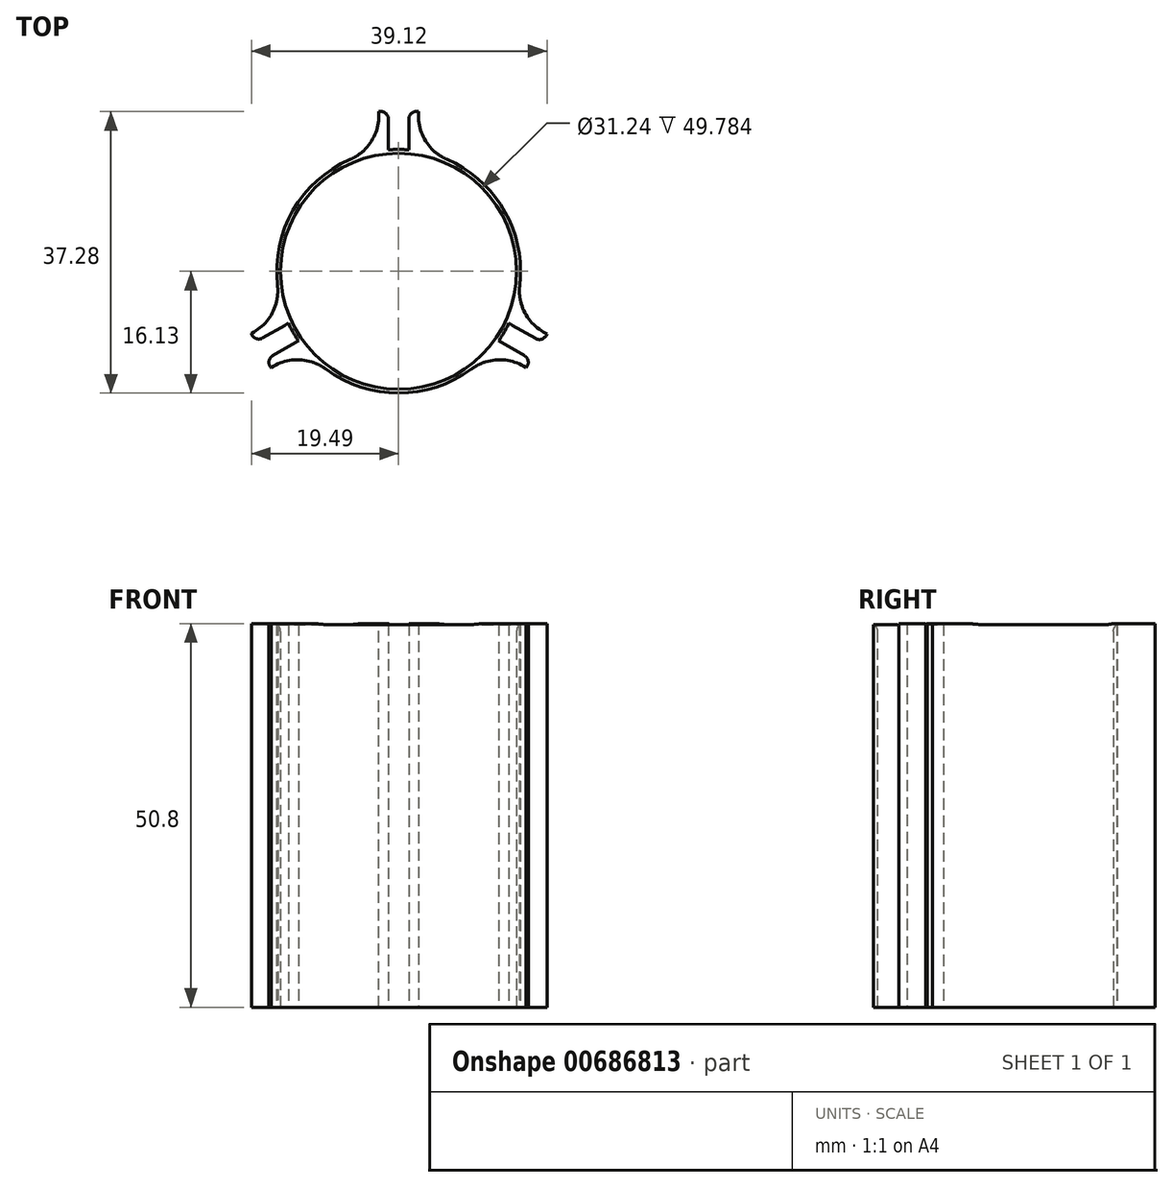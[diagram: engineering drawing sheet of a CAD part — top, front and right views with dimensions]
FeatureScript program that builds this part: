
annotation { "Feature Type Name" : "Feature", "Feature Type Description" : "" }
export const myFeature = defineFeature(function(context is Context, id is Id, definition is map)
    precondition{}
    {
        {
            var Q0;
            Q0=qCreatedBy(makeId("Top.planeOp"),FACE);
            var sketch = newSketch(context, id + "F0", { "sketchPlane" : qUnion([Q0])});
            skCircle(sketch, "E0", {"center": v(0, 0) * mm, "radius": 15.62 * mm});
            skCircle(sketch, "E1", {"center": v(0, 0) * mm, "radius": 16.13 * mm});
            skLineSegment(sketch, "E2", {"start": v(0, 0) * mm, "end": v(0, 29.54) * mm});
            skLineSegment(sketch, "E3", {"start": v(0, 0) * mm, "end": v(-29.92, -17.28) * mm});
            skLineSegment(sketch, "E4", {"start": v(0, 0) * mm, "end": v(27.94, -16.13) * mm});
            skLineSegment(sketch, "E5", {"start": v(-14.6, -6.87) * mm, "end": v(-19, -9.41) * mm});
            skLineSegment(sketch, "E6", {"start": v(-17.65, -11.74) * mm, "end": v(-13.25, -9.2) * mm});
            skPoint(sketch, "E7", {"position": v(-13.97, -8.06) * mm});
            skLineSegment(sketch, "E8", {"start": v(-15.09, -5.7) * mm, "end": v(-19.49, -8.24) * mm});
            skLineSegment(sketch, "E9", {"start": v(-19.49, -8.24) * mm, "end": v(-19, -9.41) * mm});
            skLineSegment(sketch, "E10", {"start": v(-12.48, -10.21) * mm, "end": v(-16.88, -12.75) * mm});
            skLineSegment(sketch, "E11", {"start": v(-17.65, -11.74) * mm, "end": v(-16.88, -12.75) * mm});
            skLineSegment(sketch, "E12", {"start": v(13.25, -9.2) * mm, "end": v(17.65, -11.74) * mm});
            skLineSegment(sketch, "E13", {"start": v(12.48, -10.21) * mm, "end": v(16.88, -12.75) * mm});
            skLineSegment(sketch, "E14", {"start": v(17.65, -11.74) * mm, "end": v(16.88, -12.75) * mm});
            skLineSegment(sketch, "E15", {"start": v(14.6, -6.87) * mm, "end": v(19, -9.41) * mm});
            skLineSegment(sketch, "E16", {"start": v(19, -9.41) * mm, "end": v(19.63, -8.31) * mm});
            skLineSegment(sketch, "E17", {"start": v(19.63, -8.31) * mm, "end": v(15.1, -5.7) * mm});
            skPoint(sketch, "E18", {"position": v(13.97, -8.06) * mm});
            skLineSegment(sketch, "E19", {"start": v(-1.35, 16.07) * mm, "end": v(-1.35, 21.15) * mm});
            skLineSegment(sketch, "E20", {"start": v(-1.35, 21.15) * mm, "end": v(-2.62, 21.15) * mm});
            skLineSegment(sketch, "E21", {"start": v(-2.62, 21.15) * mm, "end": v(-2.62, 15.92) * mm});
            skLineSegment(sketch, "E22", {"start": v(1.35, 16.07) * mm, "end": v(1.35, 21.15) * mm});
            skLineSegment(sketch, "E23", {"start": v(1.35, 21.15) * mm, "end": v(2.62, 21.15) * mm});
            skLineSegment(sketch, "E24", {"start": v(2.62, 21.15) * mm, "end": v(2.62, 15.92) * mm});
            skPoint(sketch, "E25", {"position": v(0, 16.13) * mm});
            skPoint(sketch, "E26", {"position": v(-1.35, 16.07) * mm});
            skSolve(sketch);
        }
        {
            var Q0;
            {var subQ0=sQuery(id+"F0.wireOp",EDGE,"E19");Q0=makeQuery(id+"F0.imprint","IMPRINT",FACE,{"disambiguationData":[TD([[makeQuery(id+"F0.imprint","IMPRINT",EDGE,{"derivedFrom":subQ0}),1.0]])]});}
            var Q1;
            {var subQ0=sQuery(id+"F0.wireOp",EDGE,"E22");Q1=makeQuery(id+"F0.imprint","IMPRINT",FACE,{"disambiguationData":[TD([[makeQuery(id+"F0.imprint","IMPRINT",EDGE,{"derivedFrom":subQ0}),-1.0]])]});}
            var Q2;
            {var subQ5=sQuery(id+"F0.wireOp",EDGE,"E2");var subQ8=sQuery(id+"F0.wireOp",EDGE,"E0");var subQ9=makeQuery(id+"F0.imprint","INTERSECT",VERTEX,{"derivedFrom":[subQ8,subQ5]});Q2=makeQuery(id+"F0.imprint","IMPRINT",FACE,{"disambiguationData":[TD([[makeQuery(id+"F0.imprint","IMPRINT",EDGE,{"disambiguationData":[TD([[subQ9,1.0]])],"derivedFrom":subQ8}),-1.0]])]});}
            var Q3;
            {var subQ0=sQuery(id+"F0.wireOp",EDGE,"E15");Q3=makeQuery(id+"F0.imprint","IMPRINT",FACE,{"disambiguationData":[TD([[makeQuery(id+"F0.imprint","IMPRINT",EDGE,{"derivedFrom":subQ0}),1.0]])]});}
            var Q4;
            {var subQ0=sQuery(id+"F0.wireOp",EDGE,"E12");Q4=makeQuery(id+"F0.imprint","IMPRINT",FACE,{"disambiguationData":[TD([[makeQuery(id+"F0.imprint","IMPRINT",EDGE,{"derivedFrom":subQ0}),-1.0]])]});}
            var Q5;
            {var subQ3=sQuery(id+"F0.wireOp",EDGE,"E3");var subQ4=sQuery(id+"F0.wireOp",EDGE,"E0");var subQ5=makeQuery(id+"F0.imprint","INTERSECT",VERTEX,{"derivedFrom":[subQ4,subQ3]});Q5=makeQuery(id+"F0.imprint","IMPRINT",FACE,{"disambiguationData":[TD([[makeQuery(id+"F0.imprint","IMPRINT",EDGE,{"disambiguationData":[TD([[subQ5,-1.0]])],"derivedFrom":subQ4}),-1.0]])]});}
            var Q6;
            {var subQ0=sQuery(id+"F0.wireOp",EDGE,"E6");Q6=makeQuery(id+"F0.imprint","IMPRINT",FACE,{"disambiguationData":[TD([[makeQuery(id+"F0.imprint","IMPRINT",EDGE,{"derivedFrom":subQ0}),-1.0]])]});}
            var Q7;
            {var subQ6=sQuery(id+"F0.wireOp",EDGE,"E3");var subQ7=sQuery(id+"F0.wireOp",EDGE,"E0");var subQ8=makeQuery(id+"F0.imprint","INTERSECT",VERTEX,{"derivedFrom":[subQ7,subQ6]});Q7=makeQuery(id+"F0.imprint","IMPRINT",FACE,{"disambiguationData":[TD([[makeQuery(id+"F0.imprint","IMPRINT",EDGE,{"disambiguationData":[TD([[subQ8,1.0]])],"derivedFrom":subQ7}),-1.0]])]});}
            var Q8;
            {var subQ0=sQuery(id+"F0.wireOp",EDGE,"E5");Q8=makeQuery(id+"F0.imprint","IMPRINT",FACE,{"disambiguationData":[TD([[makeQuery(id+"F0.imprint","IMPRINT",EDGE,{"derivedFrom":subQ0}),-1.0]])]});}
            extrude(context, id + "F1", {"entities" : qUnion([Q0, Q1, Q2, Q3, Q4, Q5, Q6, Q7, Q8]), "depth" : 50.8 * mm, "offsetDistance" : 25.4 * mm});
        }
        {
            var Q0;
            Q0=makeQuery(id+"F1.opExtrude","SWEPT_EDGE",EDGE,{"disambiguationData":[OSD([sQuery(id+"F0.wireOp",EDGE,"E1"),sQuery(id+"F0.wireOp",EDGE,"E24")])]});
            var Q1;
            Q1=makeQuery(id+"F1.opExtrude","SWEPT_EDGE",EDGE,{"disambiguationData":[OSD([sQuery(id+"F0.wireOp",EDGE,"E1"),sQuery(id+"F0.wireOp",EDGE,"E17")])]});
            var Q2;
            Q2=makeQuery(id+"F1.opExtrude","SWEPT_EDGE",EDGE,{"disambiguationData":[OSD([sQuery(id+"F0.wireOp",EDGE,"E1"),sQuery(id+"F0.wireOp",EDGE,"E13")])]});
            var Q3;
            Q3=makeQuery(id+"F1.opExtrude","SWEPT_EDGE",EDGE,{"disambiguationData":[OSD([sQuery(id+"F0.wireOp",EDGE,"E1"),sQuery(id+"F0.wireOp",EDGE,"E10")])]});
            var Q4;
            Q4=makeQuery(id+"F1.opExtrude","SWEPT_EDGE",EDGE,{"disambiguationData":[OSD([sQuery(id+"F0.wireOp",EDGE,"E1"),sQuery(id+"F0.wireOp",EDGE,"E8")])]});
            var Q5;
            Q5=makeQuery(id+"F1.opExtrude","SWEPT_EDGE",EDGE,{"disambiguationData":[OSD([sQuery(id+"F0.wireOp",EDGE,"E1"),sQuery(id+"F0.wireOp",EDGE,"E21")])]});
            fillet(context, id + "F2", {"entities" : qUnion([Q0, Q1, Q2, Q3, Q4, Q5]), "radius" : 6.35 * mm, "tangentPropagation" : true, "allowEdgeOverflow" : false});
        }
        {
            var Q0;
            Q0=makeQuery(id+"F1.opExtrude","SWEPT_EDGE",EDGE,{"disambiguationData":[OSD([sQuery(id+"F0.wireOp",EDGE,"E22"),sQuery(id+"F0.wireOp",EDGE,"E23")])]});
            var Q1;
            Q1=makeQuery(id+"F1.opExtrude","SWEPT_EDGE",EDGE,{"disambiguationData":[OSD([sQuery(id+"F0.wireOp",EDGE,"E19"),sQuery(id+"F0.wireOp",EDGE,"E20")])]});
            var Q2;
            Q2=makeQuery(id+"F1.opExtrude","SWEPT_EDGE",EDGE,{"disambiguationData":[OSD([sQuery(id+"F0.wireOp",EDGE,"E5"),sQuery(id+"F0.wireOp",EDGE,"E9")])]});
            var Q3;
            Q3=makeQuery(id+"F1.opExtrude","SWEPT_EDGE",EDGE,{"disambiguationData":[OSD([sQuery(id+"F0.wireOp",EDGE,"E6"),sQuery(id+"F0.wireOp",EDGE,"E11")])]});
            var Q4;
            Q4=makeQuery(id+"F1.opExtrude","SWEPT_EDGE",EDGE,{"disambiguationData":[OSD([sQuery(id+"F0.wireOp",EDGE,"E12"),sQuery(id+"F0.wireOp",EDGE,"E14")])]});
            var Q5;
            Q5=makeQuery(id+"F1.opExtrude","SWEPT_EDGE",EDGE,{"disambiguationData":[OSD([sQuery(id+"F0.wireOp",EDGE,"E15"),sQuery(id+"F0.wireOp",EDGE,"E16")])]});
            fillet(context, id + "F3", {"entities" : qUnion([Q0, Q1, Q2, Q3, Q4, Q5]), "radius" : 1.02 * mm, "tangentPropagation" : true, "allowEdgeOverflow" : false});
        }
        {
            var Q0;
            Q0=makeQuery(id+"F1.opExtrude","CAP_EDGE",EDGE,{"disambiguationData":[OSD([sQuery(id+"F0.wireOp",EDGE,"E0")])],"isStart":false});
            fillet(context, id + "F4", {"entities" : qUnion([Q0]), "radius" : 1.02 * mm, "tangentPropagation" : true, "allowEdgeOverflow" : false});
        }
    });
